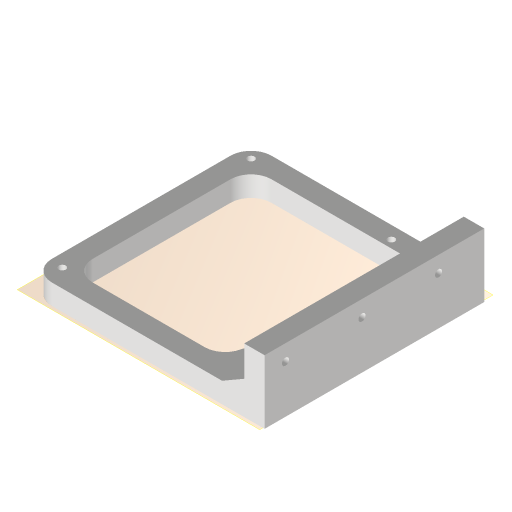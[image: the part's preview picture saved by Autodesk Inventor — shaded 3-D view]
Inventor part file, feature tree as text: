
AUTODESK INVENTOR PART (.ipt)
format: ipt  version: 2024.1 (Build 281209000, 209)  size: 250,880 bytes
history: native  units: mm
features: reference x4, sketch x3, other x3, extrude x2, plane x1, chamfer x1, fillet x1, hole x1
ambient origin geometry x8: Origin, YZ Plane, XZ Plane, XY Plane, X Axis, Y Axis, Z Axis, Center Point
bodies: Volumenkörper1 (feature_tree)
feature tree (16):
  plane  "Arbeitsebene1"
  extrude  "Extrusion1"  Depth=8.0mm
  extrude  "Extrusion2"  Depth=2.8mm
  chamfer  "Fasen1"  Distance=8.0mm
  fillet  "Rundung1"  Radius=17.0mm
  hole  "Bohrung1"  [1 undecoded]
  sketch  "Skizze1"  dims[d0=8.0mm d1=2.8mm]
  reference  "Referenz1"
  reference  "Referenz2"
  sketch  "Skizze2"  dims[d2=2.8mm d3=2.8mm]
  reference  "Referenz3"
  sketch  "Skizze3"  dims[d4=2.8mm d5=8.0mm d6=0.0mm d7=17.0mm d8=8.0mm d9=0.0mm d10=5.0mm d11=2.0mm d12=60.0deg d13=8.0mm d14=2.8mm d15=6.0mm d16=4.0mm d17=2.0mm d18=90.0deg d19=20.0mm d20=0.0mm]
  reference  "Referenz4"
  other  "Assembly_Planktoscope_Uc2version_wormdrive_V3.iam"
  other  "00_UC2_ESP32-cnc_v3:1"
  other  "60_Planktoscope_MicroscopeHolder_Bottom_v0:1"
note: 1 required parameter value undecoded (feature->parameter linkage not recoverable at this tier; creation-order binding heuristic only, values carry confidence <= 0.55)
